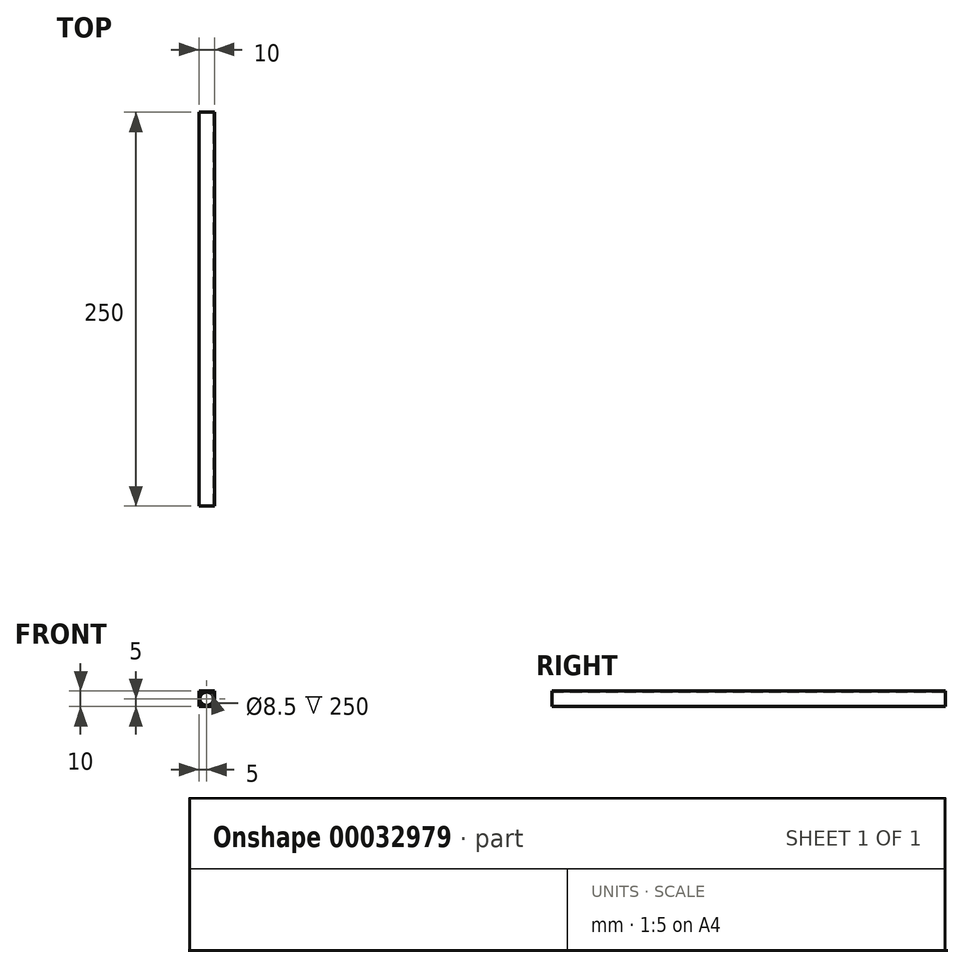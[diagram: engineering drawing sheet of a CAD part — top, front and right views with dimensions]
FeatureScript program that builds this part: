
annotation { "Feature Type Name" : "Feature", "Feature Type Description" : "" }
export const myFeature = defineFeature(function(context is Context, id is Id, definition is map)
    precondition{}
    {
        {
            var Q0;
            Q0=qCreatedBy(makeId("Front.planeOp"),FACE);
            var sketch = newSketch(context, id + "F0", { "sketchPlane" : qUnion([Q0])});
            skCircle(sketch, "E0", {"center": v(0, 0) * mm, "radius": 4.25 * mm});
            skLineSegment(sketch, "E1.rect.bottom", {"start": v(4.5, -5) * mm, "end": v(-4.5, -5) * mm});
            skLineSegment(sketch, "E1.rect.top", {"start": v(4.5, 5) * mm, "end": v(-4.5, 5) * mm});
            skLineSegment(sketch, "E1.rect.left", {"start": v(5, -4.5) * mm, "end": v(5, 4.5) * mm});
            skLineSegment(sketch, "E1.rect.right", {"start": v(-5, -4.5) * mm, "end": v(-5, 4.5) * mm});
            skPoint(sketch, "E2.visualSharp", {"position": v(-5, 5) * mm});
            skPoint(sketch, "E3.visualSharp", {"position": v(5, 5) * mm});
            skPoint(sketch, "E4.visualSharp", {"position": v(-5, -5) * mm});
            skPoint(sketch, "E5.visualSharp", {"position": v(5, -5) * mm});
            skLineSegment(sketch, "E6", {"start": v(-4.5, 5) * mm, "end": v(-5, 5) * mm});
            skLineSegment(sketch, "E7", {"start": v(-5, 4.5) * mm, "end": v(-5, 5) * mm});
            skLineSegment(sketch, "E8", {"start": v(4.5, 5) * mm, "end": v(5, 5) * mm});
            skLineSegment(sketch, "E9", {"start": v(5, 5) * mm, "end": v(5, 4.5) * mm});
            skLineSegment(sketch, "E10", {"start": v(5, -4.5) * mm, "end": v(5, -5) * mm});
            skLineSegment(sketch, "E11", {"start": v(4.5, -5) * mm, "end": v(5, -5) * mm});
            skLineSegment(sketch, "E12", {"start": v(-5, -5) * mm, "end": v(-4.5, -5) * mm});
            skLineSegment(sketch, "E13", {"start": v(-5, -4.5) * mm, "end": v(-5, -5) * mm});
            skSolve(sketch);
        }
        {
            var Q0;
            Q0=makeQuery(id+"F0.imprint","IMPRINT",FACE,{"disambiguationData":[TD([[makeQuery(id+"F0.imprint","IMPRINT",EDGE,{"derivedFrom":sQuery(id+"F0.wireOp",EDGE,"E0")}),-1.0]])]});
            extrude(context, id + "F1", {"entities" : qUnion([Q0]), "depth" : 250 * mm});
        }
    });
